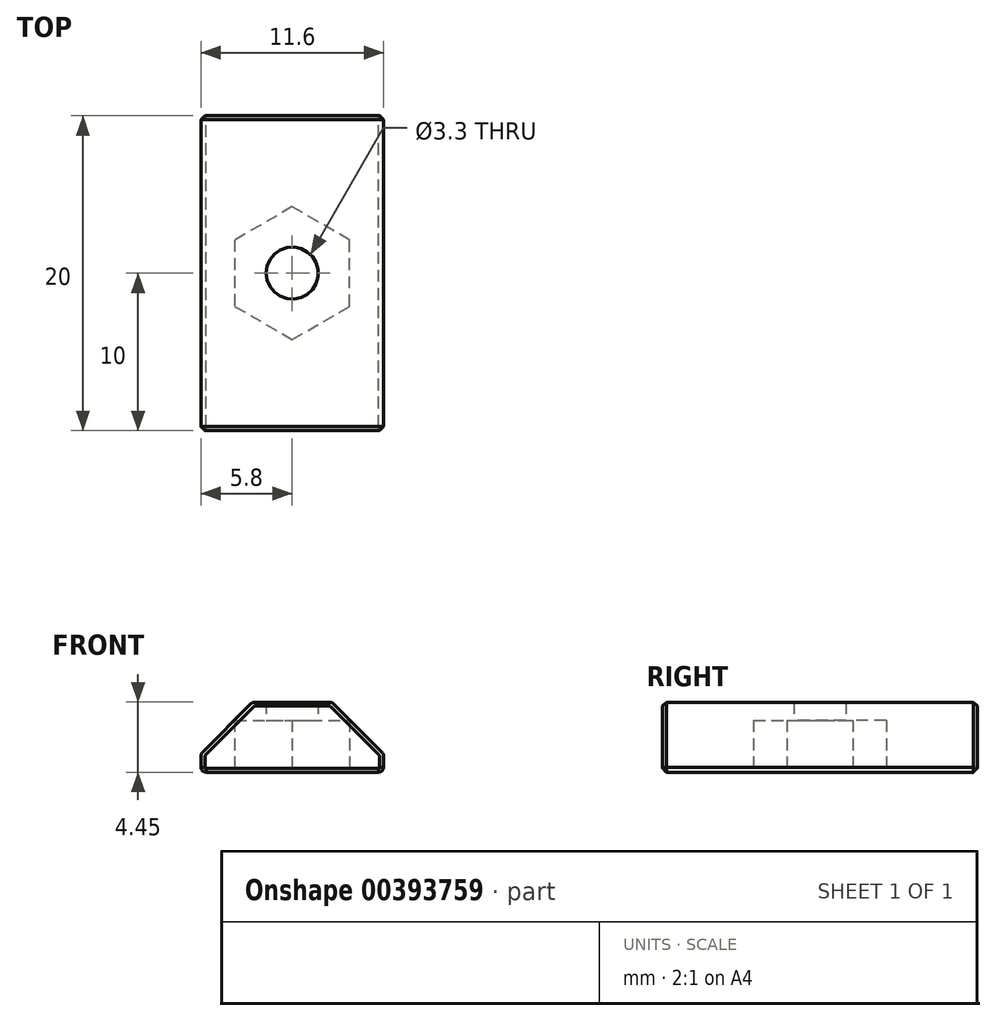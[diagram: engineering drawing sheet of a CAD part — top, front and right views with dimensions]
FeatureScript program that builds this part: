
annotation { "Feature Type Name" : "Feature", "Feature Type Description" : "" }
export const myFeature = defineFeature(function(context is Context, id is Id, definition is map)
    precondition{}
    {
        {
            var Q0;
            Q0=qCreatedBy(makeId("Front.planeOp"),FACE);
            var sketch = newSketch(context, id + "F0", { "sketchPlane" : qUnion([Q0])});
            skLineSegment(sketch, "E0.0", {"start": v(-2.67, 4.42) * mm, "end": v(-5.77, 1.32) * mm, "construction": true});
            skArc(sketch, "E1.0", {"start": v(-5.77, 1.32) * mm, "mid": v(-5.86, 1.19) * mm, "end": v(-5.9, 1.03) * mm, "construction": true});
            skLineSegment(sketch, "E2.0", {"start": v(-5.9, 1.03) * mm, "end": v(-5.9, 0.3) * mm, "construction": true});
            skArc(sketch, "E3.0", {"start": v(-5.9, 0.3) * mm, "mid": v(-5.77, 0.02) * mm, "end": v(-5.49, -0.1) * mm, "construction": true});
            skLineSegment(sketch, "E4.0", {"start": v(-5.49, -0.1) * mm, "end": v(-3.14, -0.1) * mm, "construction": true});
            skLineSegment(sketch, "E5.0", {"start": v(3.14, -0.1) * mm, "end": v(5.49, -0.1) * mm, "construction": true});
            skArc(sketch, "E6.0", {"start": v(5.49, -0.1) * mm, "mid": v(5.77, 0.02) * mm, "end": v(5.9, 0.3) * mm, "construction": true});
            skLineSegment(sketch, "E7.0", {"start": v(5.9, 0.3) * mm, "end": v(5.9, 1.03) * mm, "construction": true});
            skArc(sketch, "E8.0", {"start": v(5.9, 1.03) * mm, "mid": v(5.86, 1.19) * mm, "end": v(5.77, 1.32) * mm, "construction": true});
            skLineSegment(sketch, "E9.0", {"start": v(5.77, 1.32) * mm, "end": v(2.67, 4.42) * mm, "construction": true});
            skArc(sketch, "E10.0", {"start": v(2.67, 4.42) * mm, "mid": v(2.54, 4.51) * mm, "end": v(2.38, 4.55) * mm, "construction": true});
            skLineSegment(sketch, "E11.0", {"start": v(2.38, 4.55) * mm, "end": v(-2.38, 4.55) * mm, "construction": true});
            skArc(sketch, "E12.0", {"start": v(-2.38, 4.55) * mm, "mid": v(-2.54, 4.51) * mm, "end": v(-2.67, 4.42) * mm, "construction": true});
            skLineSegment(sketch, "E13.0", {"start": v(5.7, 1.25) * mm, "end": v(2.6, 4.35) * mm});
            skLineSegment(sketch, "E14.0", {"start": v(2.38, 4.45) * mm, "end": v(-2.38, 4.45) * mm});
            skLineSegment(sketch, "E15.0", {"start": v(-2.6, 4.35) * mm, "end": v(-5.7, 1.25) * mm});
            skLineSegment(sketch, "E16.0", {"start": v(-5.8, 1.03) * mm, "end": v(-5.8, 0.3) * mm});
            skLineSegment(sketch, "E17.0", {"start": v(-5.49, 0) * mm, "end": v(5.49, 0) * mm});
            skLineSegment(sketch, "E18.0", {"start": v(5.8, 0.3) * mm, "end": v(5.8, 1.03) * mm});
            skArc(sketch, "E19.0", {"start": v(-5.8, 0.3) * mm, "mid": v(-5.7, 0.1) * mm, "end": v(-5.49, 0) * mm});
            skArc(sketch, "E20.0", {"start": v(-5.7, 1.25) * mm, "mid": v(-5.77, 1.15) * mm, "end": v(-5.8, 1.03) * mm});
            skArc(sketch, "E21.0", {"start": v(-2.38, 4.45) * mm, "mid": v(-2.5, 4.42) * mm, "end": v(-2.6, 4.35) * mm});
            skArc(sketch, "E22.0", {"start": v(2.6, 4.35) * mm, "mid": v(2.5, 4.42) * mm, "end": v(2.38, 4.45) * mm});
            skArc(sketch, "E23.0", {"start": v(5.8, 1.03) * mm, "mid": v(5.77, 1.15) * mm, "end": v(5.7, 1.25) * mm});
            skArc(sketch, "E24.0", {"start": v(5.49, 0) * mm, "mid": v(5.7, 0.1) * mm, "end": v(5.8, 0.3) * mm});
            skPoint(sketch, "E25", {"position": v(0, 0) * mm});
            skSolve(sketch);
        }
        {
            var Q0;
            Q0 = qSketchRegion(id + "F0", true);
            extrude(context, id + "F1", {"entities" : qUnion([Q0]), "depth" : 20 * mm});
        }
        {
            var Q0;
            Q0=qCreatedBy(makeId("Top.planeOp"),FACE);
            var sketch = newSketch(context, id + "F2", { "sketchPlane" : qUnion([Q0])});
            skPoint(sketch, "E26", {"position": v(0, -10) * mm});
            skSolve(sketch);
        }
        {
            var Q0;
            Q0=sQuery(id+"F2.wireOp",VERTEX,"E26");
            var Q1;
            Q1=makeQuery(id+"F1.opExtrude","SWEPT_BODY",BODY,{"disambiguationData":[OSD([sQuery(id+"F0.wireOp",EDGE,"E13.0"),sQuery(id+"F0.wireOp",EDGE,"E14.0"),sQuery(id+"F0.wireOp",EDGE,"E15.0"),sQuery(id+"F0.wireOp",EDGE,"E16.0"),sQuery(id+"F0.wireOp",EDGE,"E17.0"),sQuery(id+"F0.wireOp",EDGE,"E18.0"),sQuery(id+"F0.wireOp",EDGE,"E19.0"),sQuery(id+"F0.wireOp",EDGE,"E20.0"),sQuery(id+"F0.wireOp",EDGE,"E21.0"),sQuery(id+"F0.wireOp",EDGE,"E22.0"),sQuery(id+"F0.wireOp",EDGE,"E23.0"),sQuery(id+"F0.wireOp",EDGE,"E24.0")])]});
            hole(context, id + "F3", {"style" : HoleStyle.SIMPLE, "endStyle" : HoleEndStyle.THROUGH, "oppositeDirection" : true, "standardTappedOrClearance" : lookupTablePath({ "standard" : "ISO", "engagement" : "75%", "pitch" : "0.7 mm", "size" : "M4", "type" : "Tapped" }), "standardBlindInLast" : lookupTablePath({ "standard" : "ISO", "engagement" : "75%", "pitch" : "0.7 mm", "size" : "M4", "type" : "Tapped" }), "holeDiameter" : 3.3 * mm, "showTappedDepth" : true, "isTappedThrough" : true, "tappedDepth" : 12 * mm, "tapClearance" : 3, "locations" : qUnion([Q0]), "scope" : qUnion([Q1]), "majorDiameter" : 4 * mm});
        }
        {
            var Q0;
            Q0=makeQuery(id+"F1.opExtrude","SWEPT_FACE",FACE,{"disambiguationData":[OSD([sQuery(id+"F0.wireOp",EDGE,"E17.0")])]});
            var sketch = newSketch(context, id + "F4", { "sketchPlane" : qUnion([Q0])});
            skCircle(sketch, "E27.cCircle", {"center": v(0, 10) * mm, "radius": 3.65 * mm, "construction": true});
            skLineSegment(sketch, "E27.0", {"start": v(3.65, 12.1) * mm, "end": v(3.65, 7.9) * mm});
            skLineSegment(sketch, "E27.1", {"start": v(3.65, 7.9) * mm, "end": v(0, 5.79) * mm});
            skLineSegment(sketch, "E27.2", {"start": v(0, 5.79) * mm, "end": v(-3.65, 7.9) * mm});
            skLineSegment(sketch, "E27.3", {"start": v(-3.65, 7.9) * mm, "end": v(-3.65, 12.1) * mm});
            skLineSegment(sketch, "E27.4", {"start": v(-3.65, 12.1) * mm, "end": v(0, 14.21) * mm});
            skLineSegment(sketch, "E27.5", {"start": v(0, 14.21) * mm, "end": v(3.65, 12.1) * mm});
            skPoint(sketch, "E27.0.midPoint", {"position": v(3.65, 10) * mm});
            skSolve(sketch);
        }
        {
            var Q0;
            Q0 = qSketchRegion(id + "F4", true);
            extrude(context, id + "F5", {"entities" : qUnion([Q0]), "operationType" : NewBodyOperationType.REMOVE, "oppositeDirection" : true, "depth" : 3.3 * mm});
        }
        {
            var Q0;
            Q0=makeQuery(id+"F5.boolean.opBoolean","COPY",EDGE,{"derivedFrom":makeQuery(id+"F5.opExtrude","CAP_EDGE",EDGE,{"disambiguationData":[OSD([sQuery(id+"F4.wireOp",EDGE,"E27.5")])],"isStart":true})});
            var Q1;
            Q1=makeQuery(id+"F5.boolean.opBoolean","COPY",EDGE,{"derivedFrom":makeQuery(id+"F5.opExtrude","CAP_EDGE",EDGE,{"disambiguationData":[OSD([sQuery(id+"F4.wireOp",EDGE,"E27.0")])],"isStart":true})});
            var Q2;
            Q2=makeQuery(id+"F5.boolean.opBoolean","COPY",EDGE,{"derivedFrom":makeQuery(id+"F5.opExtrude","CAP_EDGE",EDGE,{"disambiguationData":[OSD([sQuery(id+"F4.wireOp",EDGE,"E27.1")])],"isStart":true})});
            var Q3;
            Q3=makeQuery(id+"F5.boolean.opBoolean","COPY",EDGE,{"derivedFrom":makeQuery(id+"F5.opExtrude","CAP_EDGE",EDGE,{"disambiguationData":[OSD([sQuery(id+"F4.wireOp",EDGE,"E27.2")])],"isStart":true})});
            var Q4;
            Q4=makeQuery(id+"F5.boolean.opBoolean","COPY",EDGE,{"derivedFrom":makeQuery(id+"F5.opExtrude","CAP_EDGE",EDGE,{"disambiguationData":[OSD([sQuery(id+"F4.wireOp",EDGE,"E27.3")])],"isStart":true})});
            var Q5;
            Q5=makeQuery(id+"F5.boolean.opBoolean","COPY",EDGE,{"derivedFrom":makeQuery(id+"F5.opExtrude","CAP_EDGE",EDGE,{"disambiguationData":[OSD([sQuery(id+"F4.wireOp",EDGE,"E27.4")])],"isStart":true})});
            var Q6;
            Q6=makeQuery(id+"F1.opExtrude","CAP_EDGE",EDGE,{"disambiguationData":[OSD([sQuery(id+"F0.wireOp",EDGE,"E14.0")])],"isStart":false});
            var Q7;
            Q7=makeQuery(id+"F1.opExtrude","CAP_EDGE",EDGE,{"disambiguationData":[OSD([sQuery(id+"F0.wireOp",EDGE,"E13.0")])],"isStart":false});
            var Q8;
            Q8=makeQuery(id+"F1.opExtrude","CAP_EDGE",EDGE,{"disambiguationData":[OSD([sQuery(id+"F0.wireOp",EDGE,"E17.0")])],"isStart":false});
            var Q9;
            Q9=makeQuery(id+"F1.opExtrude","CAP_EDGE",EDGE,{"disambiguationData":[OSD([sQuery(id+"F0.wireOp",EDGE,"E17.0")])],"isStart":true});
            var Q10;
            Q10=makeQuery(id+"F1.opExtrude","CAP_EDGE",EDGE,{"disambiguationData":[OSD([sQuery(id+"F0.wireOp",EDGE,"E16.0")])],"isStart":true});
            chamfer(context, id + "F6", {"entities" : qUnion([Q0, Q1, Q2, Q3, Q4, Q5, Q6, Q7, Q8, Q9, Q10]), "width" : .25 * mm, "tangentPropagation" : true});
        }
    });
